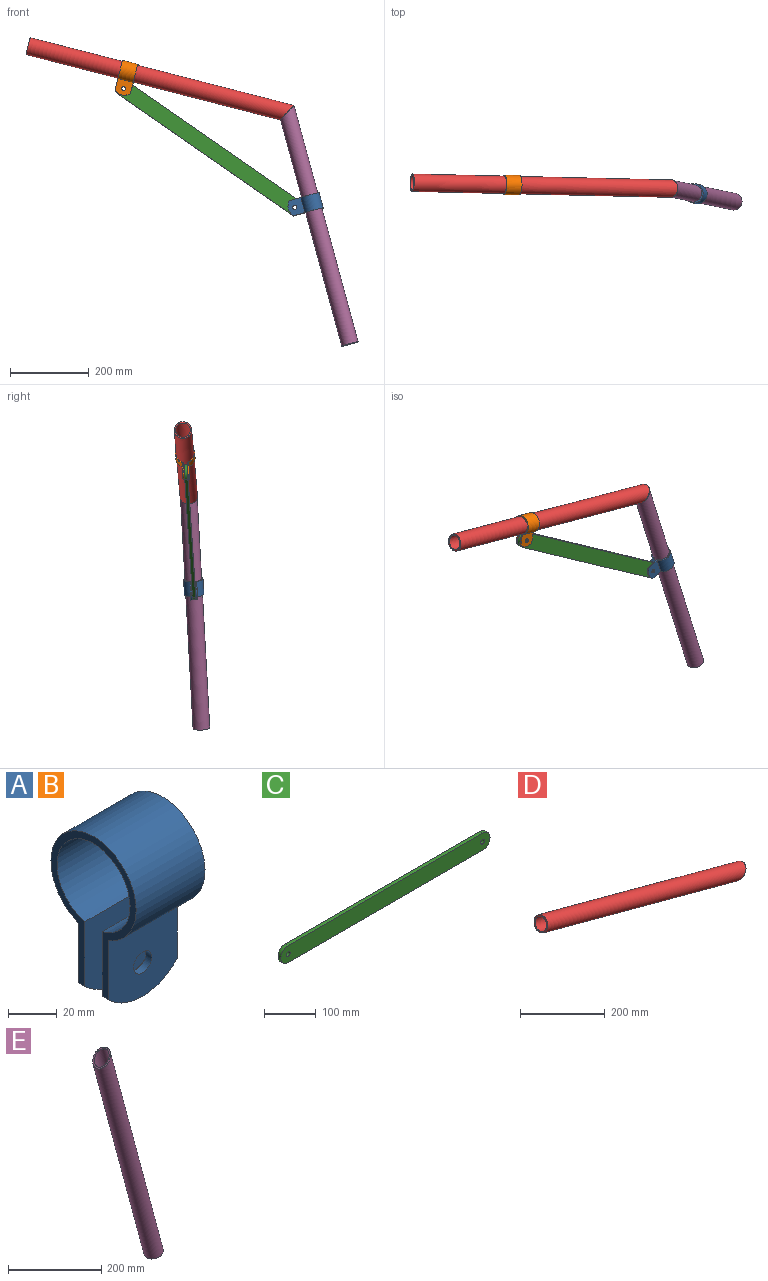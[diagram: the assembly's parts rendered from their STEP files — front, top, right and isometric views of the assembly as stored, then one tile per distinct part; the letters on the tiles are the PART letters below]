
ASSEMBLY  parts=5 mates=5
PART A: 12 faces, bbox 40x49.4x86 mm
  f0: plane 40x38.11mm, normal (0,1,0), area 1331mm2, adj f3,f6,f7,f8,f11
  f1: plane 40.7x40mm, normal (0,1,0), area 1434.5mm2, adj f5,f6,f7,f9,f10
  f2: plane 40.7x40mm, normal (0,-1,0), area 1434.5mm2, adj f5,f6,f7,f8,f11
  f3: cylinder r=24.7mm len=49.4mm, axis (-1,0,0), area 5513.6mm2, adj f0,f4,f6,f7
  f4: plane 40x38.11mm, normal (0,-1,0), area 1331mm2, adj f3,f6,f7,f9,f10
  f5: cylinder r=21.2mm len=42.4mm, axis (-1,0,0), area 4924.3mm2, adj f1,f2,f6,f7
  f6: plane 77.01x49.4mm, normal (1,0,0), area 669.4mm2, adj f0,f1,f2,f3,f4,f5,f8,f9
  f7: plane 77.73x49.4mm, normal (-1,0,0), area 674.5mm2, adj f0,f1,f2,f3,f4,f5,f8,f9
  f8: cylinder r=27.5mm len=40mm, axis (0,-1,0), area 156.8mm2, adj f0,f2,f6,f7
  f9: cylinder r=27.5mm len=40mm, axis (0,-1,0), area 156.8mm2, adj f1,f4,f6,f7
  f10: cylinder r=5.25mm len=10.5mm, axis (0,-1,0), area 115.5mm2, adj f1,f4
  f11: cylinder r=5.25mm len=10.5mm, axis (0,-1,0), area 115.5mm2, adj f0,f2
PART B: same geometry as A
PART C: 8 faces, bbox 570x8x40 mm
  f0: plane 530x8mm, normal (0,0,1), area 4240mm2, adj f2,f3,f5,f6
  f1: plane 530x8mm, normal (0,0,-1), area 4240mm2, adj f2,f3,f5,f6
  f2: plane 570x40mm, normal (0,-1,0), area 22283.5mm2, adj f0,f1,f4,f5,f6,f7
  f3: plane 570x40mm, normal (0,1,0), area 22283.5mm2, adj f0,f1,f4,f5,f6,f7
  f4: cylinder r=5.25mm len=10.5mm, axis (0,-1,0), area 263.9mm2, adj f2,f3
  f5: cylinder r=20mm len=40mm, axis (0,-1,0), area 502.7mm2, adj f0,f1,f2,f3
  f6: cylinder r=20mm len=40mm, axis (0,-1,0), area 502.7mm2, adj f0,f1,f2,f3
  f7: cylinder r=5.25mm len=10.5mm, axis (0,-1,0), area 263.9mm2, adj f2,f3
PART D: 4 faces, bbox 679.6x44.2x221.7 mm
  f0: cylinder r=22.1mm len=679.61mm, axis (-0.97,0,0.26), area 94404mm2, adj f2,f3
  f1: cylinder r=18.6mm len=675.98mm, axis (-0.97,0,0.26), area 79453.1mm2, adj f2,f3
  f2: plane 44.2x42.69mm, normal (-0.97,0,0.26), area 447.5mm2, adj f0,f1
  f3: plane 44.2x36.63mm, normal (0.73,0,-0.68), area 506.6mm2, adj f0,f1
PART E: 5 faces, bbox 202.7x42.8x613.5 mm
  f0: cylinder r=21.2mm len=613.08mm, axis (-0.26,0,0.97), area 81236mm2, adj f1,f3,f4
  f1: plane 42.4x40.96mm, normal (0.26,0,-0.97), area 427.7mm2, adj f0,f2
  f2: cylinder r=17.7mm len=609.13mm, axis (-0.26,0,0.97), area 67823.5mm2, adj f1,f3
  f3: plane 42.4x36.73mm, normal (-0.74,0,0.68), area 504.9mm2, adj f0,f2,f4
  f4: plane 8.15x0.81mm, normal (0.26,0,0.97), area 2.1mm2, adj f0,f3
PLACE A rot(axis=(-0.03,1,-0.03),74.9deg) t=(58.76,46.23,-356.11)mm
PLACE B rot(axis=(-0.2,0.98,-0.06),14.7deg) t=(-408.11,67.86,-22.93)mm
PLACE C rot(axis=(-0.08,1,-0.04),34.9deg) t=(-393.87,67.39,-29.44)mm
PLACE D rot(axis=(-0.97,-0.19,-0.16),3.1deg) t=(-468.04,69.21,-7.54)mm
PLACE E rot(axis=(-0.98,-0.05,-0.17),3deg) t=(-467.21,69.39,-3.96)mm
MATE fastened D.f3 <-> E.f3  axis (0.74,-0.04,-0.67) through (-3.36,58.75,-126.84)mm
MATE cylindrical B.f5 <-> D.f0  axis (-0.97,0.02,0.25) through (-408.11,67.86,-22.93)mm
MATE revolute A.f10 <-> C.f5  axis (0.01,1,-0.05) through (15.96,41.03,-367.43)mm
MATE cylindrical A.f5 <-> E.f0  axis (-0.26,0.05,0.96) through (63.99,45.18,-375.39)mm
MATE revolute B.f10 <-> C.f4  axis (-0.01,-1,0.05) through (-419.23,57.24,-65.34)mm
